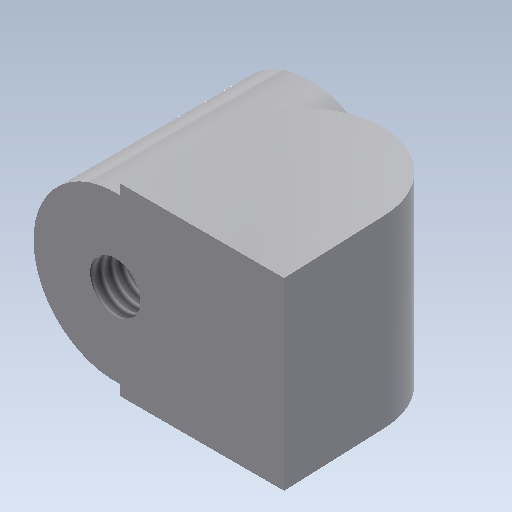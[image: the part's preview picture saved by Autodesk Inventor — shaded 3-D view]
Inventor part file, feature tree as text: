
AUTODESK INVENTOR PART (.ipt)
format: ipt  version: 2020 (Build 240168000, 168)  size: 126,464 bytes
history: native  units: mm
features: extrude x2, hole x2, sketch x2
ambient origin geometry x8: Origin, YZ Plane, XZ Plane, XY Plane, X Axis, Y Axis, Z Axis, Center Point
bodies: Solid1 (feature_tree)
feature tree (6):
  extrude  "Extrusion1"  Depth=5.0mm
  extrude  "Extrusion2"  Depth=9.0mm TaperAngle=0.0deg
  hole  "Hole2"  [1 undecoded]
  hole  "Hole3"  [1 undecoded]
  sketch  "Sketch1"  dims[d0=3.8mm d1=5.0mm]
  sketch  "Sketch2"  dims[d2=8.0mm d3=9.0mm d4=0.0mm d5=8.0mm d6=4.25mm d7=9.5mm d8=0.0mm d18=10.0mm d19=10.0mm d20=2.459mm d21=6.0mm d22=4.0mm d23=2.0mm d24=90.0deg d25=12.05mm d26=0.0mm d27=10.0mm d28=10.0mm d29=3.0mm d30=6.0mm d31=4.0mm d32=2.0mm d33=90.0deg d34=6.0mm d35=0.0mm]
note: 2 required parameter values undecoded (feature->parameter linkage not recoverable at this tier; creation-order binding heuristic only, values carry confidence <= 0.55)
